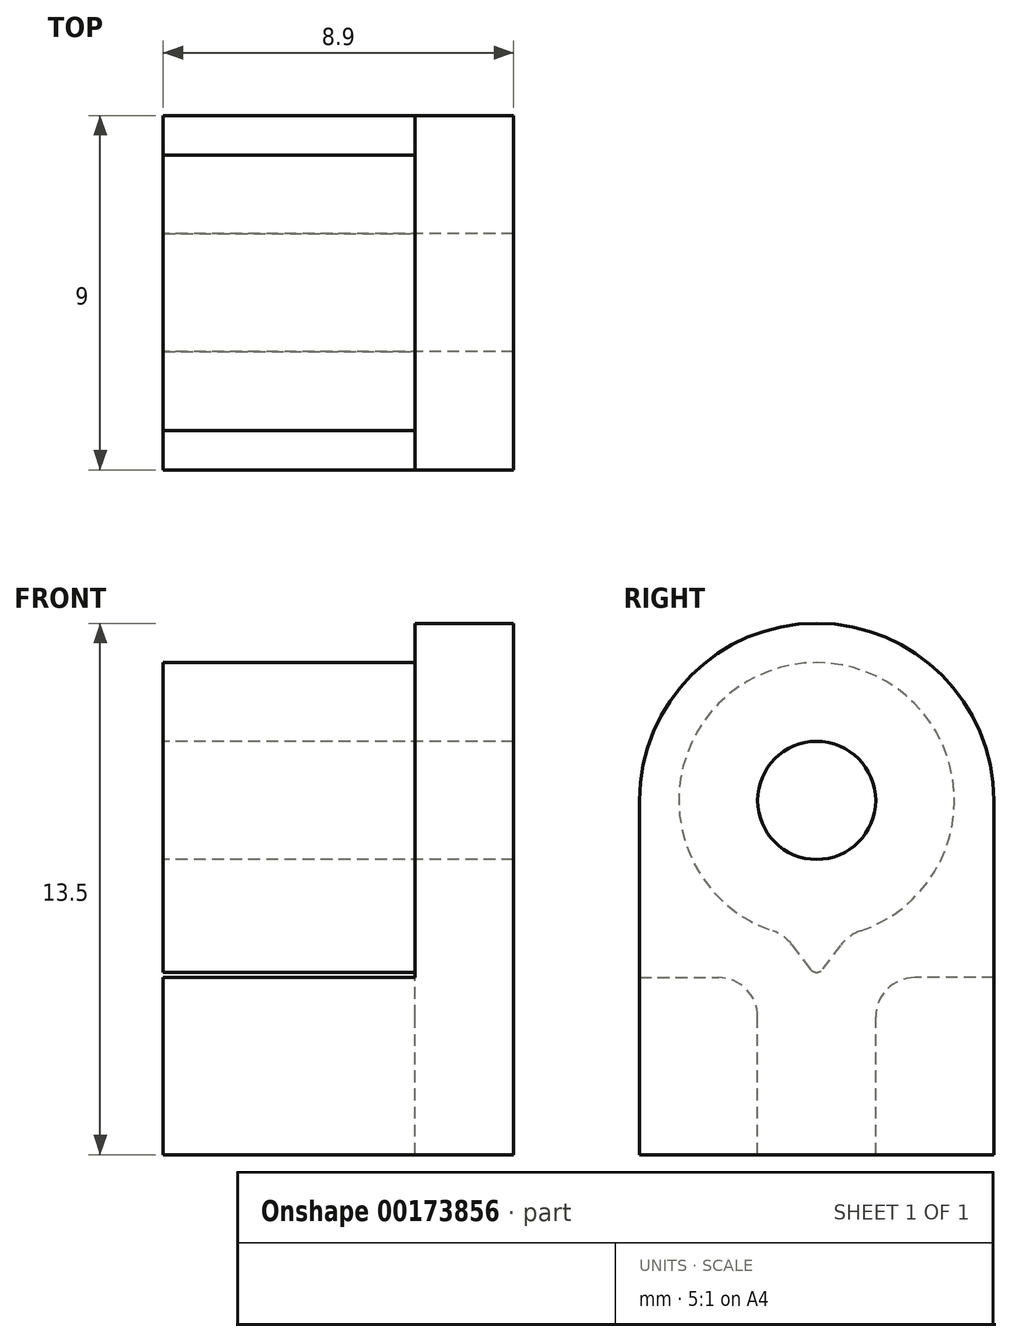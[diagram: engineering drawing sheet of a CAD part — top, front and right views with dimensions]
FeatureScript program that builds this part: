
annotation { "Feature Type Name" : "Feature", "Feature Type Description" : "" }
export const myFeature = defineFeature(function(context is Context, id is Id, definition is map)
    precondition{}
    {
        {
            var Q0;
            Q0=qCreatedBy(makeId("Right.planeOp"),FACE);
            var sketch = newSketch(context, id + "F0", { "sketchPlane" : qUnion([Q0])});
            skLineSegment(sketch, "E0.bottom", {"start": v(4.5, -4.5) * mm, "end": v(-4.5, -4.5) * mm});
            skLineSegment(sketch, "E0.top", {"start": v(4.5, 4.5) * mm, "end": v(-4.5, 4.5) * mm});
            skLineSegment(sketch, "E0.left", {"start": v(4.5, -4.5) * mm, "end": v(4.5, 4.5) * mm});
            skLineSegment(sketch, "E0.right", {"start": v(-4.5, -4.5) * mm, "end": v(-4.5, 4.5) * mm});
            skPoint(sketch, "E0.middle", {"position": v(0, 0) * mm});
            skCircle(sketch, "E1", {"center": v(0, 4.5) * mm, "radius": 4.5 * mm});
            skCircle(sketch, "E2", {"center": v(0, 4.5) * mm, "radius": 1.5 * mm});
            skSolve(sketch);
        }
        {
            var Q0;
            {var subQ1=sQuery(id+"F0.wireOp",EDGE,"E0.top");var subQ3=sQuery(id+"F0.wireOp",EDGE,"E2");var subQ4=makeQuery(id+"F0.imprint","INTERSECT",VERTEX,{"disambiguationData":[OD(0.0)],"derivedFrom":[subQ1,subQ3]});Q0=makeQuery(id+"F0.imprint","IMPRINT",FACE,{"disambiguationData":[TD([[makeQuery(id+"F0.imprint","IMPRINT",EDGE,{"disambiguationData":[TD([[subQ4,1.0]])],"derivedFrom":subQ3}),-1.0]])]});}
            var Q1;
            {var subQ1=sQuery(id+"F0.wireOp",EDGE,"E0.top");var subQ3=sQuery(id+"F0.wireOp",EDGE,"E2");var subQ4=makeQuery(id+"F0.imprint","INTERSECT",VERTEX,{"disambiguationData":[OD(0.0)],"derivedFrom":[subQ1,subQ3]});Q1=makeQuery(id+"F0.imprint","IMPRINT",FACE,{"disambiguationData":[TD([[makeQuery(id+"F0.imprint","IMPRINT",EDGE,{"disambiguationData":[TD([[subQ4,-1.0]])],"derivedFrom":subQ3}),-1.0]])]});}
            var Q2;
            Q2=makeQuery(id+"F0.imprint","IMPRINT",FACE,{"disambiguationData":[TD([[makeQuery(id+"F0.imprint","IMPRINT",EDGE,{"derivedFrom":sQuery(id+"F0.wireOp",EDGE,"E0.bottom")}),-1.0]])]});
            extrude(context, id + "F1", {"entities" : qUnion([Q0, Q1, Q2]), "depth" : 2.5 * mm});
        }
        {
            var Q0;
            Q0=makeQuery(id+"F1.opExtrude","CAP_FACE",FACE,{"disambiguationData":[OSD([sQuery(id+"F0.wireOp",EDGE,"E0.bottom"),sQuery(id+"F0.wireOp",EDGE,"E0.left"),sQuery(id+"F0.wireOp",EDGE,"E0.right"),sQuery(id+"F0.wireOp",EDGE,"E1"),sQuery(id+"F0.wireOp",EDGE,"E2")])],"isStart":true});
            var sketch = newSketch(context, id + "F2", { "sketchPlane" : qUnion([Q0])});
            skCircle(sketch, "E3", {"center": v(0, 4.5) * mm, "radius": 3.5 * mm});
            skLineSegment(sketch, "E4.bottom", {"start": v(-4.5, -4.5) * mm, "end": v(-1.5, -4.5) * mm});
            skLineSegment(sketch, "E4.top", {"start": v(-4.5, 0) * mm, "end": v(-1.5, 0) * mm});
            skLineSegment(sketch, "E4.left", {"start": v(-4.5, -4.5) * mm, "end": v(-4.5, 0) * mm});
            skLineSegment(sketch, "E4.right", {"start": v(-1.5, -4.5) * mm, "end": v(-1.5, 0) * mm});
            skLineSegment(sketch, "E5.bottom", {"start": v(4.5, -4.5) * mm, "end": v(1.5, -4.5) * mm});
            skLineSegment(sketch, "E5.top", {"start": v(4.5, 0) * mm, "end": v(1.5, 0) * mm});
            skLineSegment(sketch, "E5.left", {"start": v(4.5, -4.5) * mm, "end": v(4.5, 0) * mm});
            skLineSegment(sketch, "E5.right", {"start": v(1.5, -4.5) * mm, "end": v(1.5, 0) * mm});
            skLineSegment(sketch, "E6", {"start": v(0, 4.5) * mm, "end": v(0, 0) * mm});
            skLineSegment(sketch, "E7", {"start": v(0, 0) * mm, "end": v(-1.5, 2) * mm});
            skLineSegment(sketch, "E8", {"start": v(-1.5, 2) * mm, "end": v(1.5, 2) * mm});
            skLineSegment(sketch, "E9", {"start": v(1.5, 2) * mm, "end": v(0, 0) * mm});
            skSolve(sketch);
        }
        {
            var Q0;
            Q0=makeQuery(id+"F2.imprint","IMPRINT",FACE,{"disambiguationData":[TD([[makeQuery(id+"F2.imprint","IMPRINT",EDGE,{"derivedFrom":sQuery(id+"F2.wireOp",EDGE,"E4.bottom")}),1.0]])]});
            var Q1;
            Q1=makeQuery(id+"F2.imprint","IMPRINT",FACE,{"disambiguationData":[TD([[makeQuery(id+"F2.imprint","IMPRINT",EDGE,{"derivedFrom":sQuery(id+"F2.wireOp",EDGE,"E5.bottom")}),1.0]])]});
            var Q2;
            Q2=makeQuery(id+"F2.imprint","IMPRINT",FACE,{"disambiguationData":[TD([[makeQuery(id+"F2.imprint","IMPRINT",EDGE,{"derivedFrom":sQuery(id+"F2.wireOp",EDGE,"E3")}),1.0]])]});
            var Q3;
            Q3=makeQuery(id+"F2.imprint","IMPRINT",FACE,{"disambiguationData":[TD([[makeQuery(id+"F2.imprint","IMPRINT",EDGE,{"derivedFrom":makeQuery(id+"F1.opExtrude","CAP_EDGE",EDGE,{"disambiguationData":[OSD([sQuery(id+"F0.wireOp",EDGE,"E2")])],"isStart":true})}),1.0]])]});
            var Q4;
            {var subQ0=sQuery(id+"F2.wireOp",EDGE,"E6");var subQ1=sQuery(id+"F2.wireOp",EDGE,"E3");var subQ2=makeQuery(id+"F2.imprint","INTERSECT",VERTEX,{"derivedFrom":[subQ1,subQ0]});Q4=makeQuery(id+"F2.imprint","IMPRINT",FACE,{"disambiguationData":[TD([[makeQuery(id+"F2.imprint","IMPRINT",EDGE,{"disambiguationData":[TD([[subQ2,1.0]])],"derivedFrom":subQ1}),-1.0]])]});}
            var Q5;
            {var subQ0=sQuery(id+"F2.wireOp",EDGE,"E6");var subQ1=sQuery(id+"F2.wireOp",EDGE,"E3");var subQ2=makeQuery(id+"F2.imprint","INTERSECT",VERTEX,{"derivedFrom":[subQ1,subQ0]});Q5=makeQuery(id+"F2.imprint","IMPRINT",FACE,{"disambiguationData":[TD([[makeQuery(id+"F2.imprint","IMPRINT",EDGE,{"disambiguationData":[TD([[subQ2,-1.0]])],"derivedFrom":subQ1}),-1.0]])]});}
            extrude(context, id + "F3", {"entities" : qUnion([Q0, Q1, Q2, Q3, Q4, Q5]), "operationType" : NewBodyOperationType.ADD, "depth" : 6.4 * mm});
        }
        {
            var Q0;
            Q0=makeQuery(id+"F3.opExtrude","SWEPT_EDGE",EDGE,{"disambiguationData":[OSD([sQuery(id+"F2.wireOp",EDGE,"E4.top"),sQuery(id+"F2.wireOp",EDGE,"E4.right")])]});
            var Q1;
            Q1=makeQuery(id+"F3.opExtrude","SWEPT_EDGE",EDGE,{"disambiguationData":[OSD([sQuery(id+"F2.wireOp",EDGE,"E5.top"),sQuery(id+"F2.wireOp",EDGE,"E5.right")])]});
            var Q2;
            Q2=makeQuery(id+"F3.opExtrude","SWEPT_EDGE",EDGE,{"disambiguationData":[OSD([sQuery(id+"F2.wireOp",EDGE,"E3"),sQuery(id+"F2.wireOp",EDGE,"E7")])]});
            var Q3;
            Q3=makeQuery(id+"F3.opExtrude","SWEPT_EDGE",EDGE,{"disambiguationData":[OSD([sQuery(id+"F2.wireOp",EDGE,"E3"),sQuery(id+"F2.wireOp",EDGE,"E9")])]});
            fillet(context, id + "F4", {"entities" : qUnion([Q0, Q1, Q2, Q3]), "radius" : 1 * mm, "tangentPropagation" : true, "allowEdgeOverflow" : false});
        }
        {
            var Q0;
            Q0=makeQuery(id+"F3.opExtrude","SWEPT_EDGE",EDGE,{"disambiguationData":[OSD([sQuery(id+"F2.wireOp",EDGE,"E6"),sQuery(id+"F2.wireOp",EDGE,"E7"),sQuery(id+"F2.wireOp",EDGE,"E9")])]});
            fillet(context, id + "F5", {"entities" : qUnion([Q0]), "radius" : .2 * mm, "tangentPropagation" : true, "allowEdgeOverflow" : false});
        }
    });
